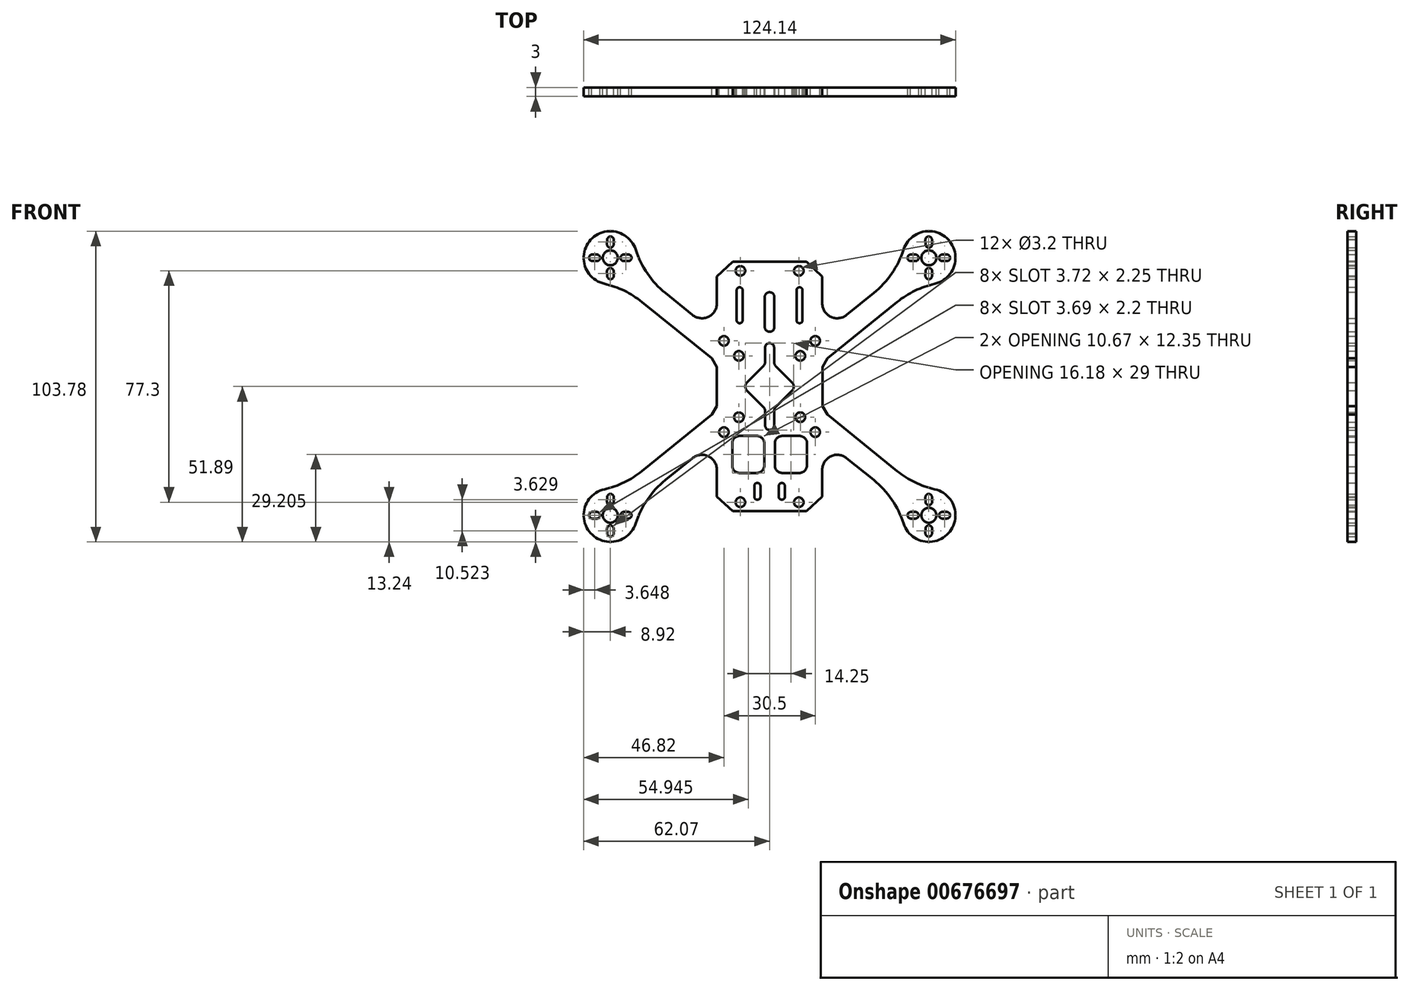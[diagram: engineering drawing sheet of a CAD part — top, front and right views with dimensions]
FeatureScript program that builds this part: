
annotation { "Feature Type Name" : "Feature", "Feature Type Description" : "" }
export const myFeature = defineFeature(function(context is Context, id is Id, definition is map)
    precondition{}
    {
        {
            var Q0;
            Q0=qCreatedBy(makeId("Front.planeOp"),FACE);
            var sketch = newSketch(context, id + "F0", { "sketchPlane" : qUnion([Q0])});
            skCircle(sketch, "E0", {"center": v(-53.17, 43) * mm, "radius": 2.5 * mm});
            skCircle(sketch, "E1", {"center": v(-53.17, 43) * mm, "radius": 4.5 * mm, "construction": true});
            skLineSegment(sketch, "E2", {"start": v(-53.17, 43) * mm, "end": v(-53.17, 56.5) * mm, "construction": true});
            skArc(sketch, "E3", {"start": v(-54.27, 47.54) * mm, "mid": v(-53.22, 46.4) * mm, "end": v(-52.08, 47.46) * mm});
            skLineSegment(sketch, "E4", {"start": v(-45.5, 43) * mm, "end": v(-53.17, 43) * mm, "construction": true});
            skArc(sketch, "E5", {"start": v(-57.69, 41.9) * mm, "mid": v(-56.58, 43) * mm, "end": v(-57.68, 44.1) * mm});
            skCircle(sketch, "E6.MirrorC", {"center": v(53.17, 43) * mm, "radius": 2.5 * mm});
            skCircle(sketch, "E7.MirrorC", {"center": v(-53.17, -43) * mm, "radius": 2.5 * mm});
            skCircle(sketch, "E8.MirrorC", {"center": v(53.17, -43) * mm, "radius": 2.5 * mm});
            skCircle(sketch, "E9", {"center": v(-53.17, 43) * mm, "radius": 40.64 * mm, "construction": true});
            skLineSegment(sketch, "E10", {"start": v(-53.17, 43) * mm, "end": v(53.17, -43) * mm, "construction": true});
            skCircle(sketch, "E11", {"center": v(-53.17, -43) * mm, "radius": 40.64 * mm, "construction": true});
            skCircle(sketch, "E12", {"center": v(53.17, 43) * mm, "radius": 40.64 * mm, "construction": true});
            skCircle(sketch, "E13", {"center": v(53.17, -43) * mm, "radius": 40.64 * mm, "construction": true});
            skPoint(sketch, "E14.visualSharp", {"position": v(-54.1, 37.74) * mm});
            skCircle(sketch, "E15", {"center": v(-53.17, 43) * mm, "radius": 7 * mm, "construction": true});
            skLineSegment(sketch, "E16", {"start": v(0, 0) * mm, "end": v(0, 56.66) * mm, "construction": true});
            skLineSegment(sketch, "E17", {"start": v(53.17, 43) * mm, "end": v(-53.17, -43) * mm, "construction": true});
            skPoint(sketch, "E18.visualSharp", {"position": v(-2.78, 0) * mm});
            skPoint(sketch, "E19.visualSharp", {"position": v(0, 2.87) * mm});
            skPoint(sketch, "E20.visualSharp", {"position": v(2.78, 0) * mm});
            skPoint(sketch, "E21.visualSharp", {"position": v(0, -2.87) * mm});
            skCircle(sketch, "E22", {"center": v(-10.25, 10.25) * mm, "radius": 1.6 * mm});
            skCircle(sketch, "E23.MirrorC", {"center": v(10.25, 10.25) * mm, "radius": 1.6 * mm});
            skCircle(sketch, "E24.MirrorC", {"center": v(-10.25, -10.25) * mm, "radius": 1.6 * mm});
            skCircle(sketch, "E25.MirrorC", {"center": v(10.25, -10.25) * mm, "radius": 1.6 * mm});
            skArc(sketch, "E26", {"start": v(0, 14.5) * mm, "mid": v(-1.06, 14.06) * mm, "end": v(-1.5, 13) * mm});
            skLineSegment(sketch, "E27", {"start": v(-1.5, 13) * mm, "end": v(-1.5, 11.17) * mm});
            skLineSegment(sketch, "E28.trimOffspring", {"start": v(-1.5, -11.66) * mm, "end": v(-1.5, -13) * mm});
            skLineSegment(sketch, "E29.filletArc", {"start": v(1.5, 11.27) * mm, "end": v(1.5, 11.27) * mm});
            skLineSegment(sketch, "E30.filletArc", {"start": v(1.5, -11.66) * mm, "end": v(1.5, -11.66) * mm});
            skLineSegment(sketch, "E31.filletArc", {"start": v(-1.5, -11.66) * mm, "end": v(-1.5, -11.66) * mm});
            skLineSegment(sketch, "E32", {"start": v(-1.5, 11.28) * mm, "end": v(-1.5, 8.22) * mm});
            skLineSegment(sketch, "E33.MirrorCS", {"start": v(1.5, 11.27) * mm, "end": v(1.5, 11.06) * mm});
            skPoint(sketch, "E34.visualSharp", {"position": v(-1.5, -11.66) * mm});
            skPoint(sketch, "E35.visualSharp", {"position": v(-1.5, 11.06) * mm});
            skPoint(sketch, "E36.newPointB", {"position": v(1.5, 11.06) * mm});
            skPoint(sketch, "E37.visualSharp", {"position": v(1.5, -11.66) * mm});
            skCircle(sketch, "E38", {"center": v(-53.17, 43) * mm, "radius": 8.8 * mm, "construction": true});
            skCircle(sketch, "E39", {"center": v(-53.17, 43) * mm, "radius": 6 * mm, "construction": true});
            skArc(sketch, "E40", {"start": v(-59.17, 44.1) * mm, "mid": v(-60.27, 43.11) * mm, "end": v(-59.4, 41.92) * mm});
            skLineSegment(sketch, "E41", {"start": v(-54.2, 49.2) * mm, "end": v(-54.27, 47.54) * mm});
            skLineSegment(sketch, "E42", {"start": v(-52.03, 49.01) * mm, "end": v(-52.08, 47.46) * mm});
            skLineSegment(sketch, "E43", {"start": v(-59.17, 44.1) * mm, "end": v(-57.68, 44.1) * mm});
            skLineSegment(sketch, "E44", {"start": v(-59.4, 41.92) * mm, "end": v(-57.69, 41.9) * mm});
            skArc(sketch, "E45.trimOffspring", {"start": v(-52.03, 49.01) * mm, "mid": v(-53.03, 50.12) * mm, "end": v(-54.2, 49.2) * mm});
            skArc(sketch, "E46.MirrorCS", {"start": v(-47.18, 44.1) * mm, "mid": v(-46.08, 43.11) * mm, "end": v(-46.96, 41.92) * mm});
            skArc(sketch, "E47.MirrorCS", {"start": v(-48.66, 41.9) * mm, "mid": v(-49.77, 43) * mm, "end": v(-48.67, 44.1) * mm});
            skLineSegment(sketch, "E48.MirrorCS", {"start": v(-47.18, 44.1) * mm, "end": v(-48.67, 44.1) * mm});
            skLineSegment(sketch, "E49.MirrorCS", {"start": v(-46.96, 41.92) * mm, "end": v(-48.66, 41.9) * mm});
            skLineSegment(sketch, "E50.MirrorCS", {"start": v(-52.03, 36.99) * mm, "end": v(-52.08, 38.54) * mm});
            skArc(sketch, "E51.MirrorCS", {"start": v(-52.03, 36.99) * mm, "mid": v(-53.03, 35.88) * mm, "end": v(-54.2, 36.8) * mm});
            skArc(sketch, "E52.MirrorCS", {"start": v(-54.27, 38.46) * mm, "mid": v(-53.22, 39.6) * mm, "end": v(-52.08, 38.54) * mm});
            skLineSegment(sketch, "E53.MirrorCS", {"start": v(-54.2, 36.8) * mm, "end": v(-54.27, 38.46) * mm});
            skLineSegment(sketch, "E54.MirrorCS", {"start": v(-52.03, -49.01) * mm, "end": v(-52.08, -47.46) * mm});
            skLineSegment(sketch, "E55.MirrorCS", {"start": v(-52.03, -36.99) * mm, "end": v(-52.08, -38.54) * mm});
            skLineSegment(sketch, "E56.MirrorCS", {"start": v(-59.4, -41.92) * mm, "end": v(-57.69, -41.9) * mm});
            skLineSegment(sketch, "E57.MirrorCS", {"start": v(-47.18, -44.1) * mm, "end": v(-48.67, -44.1) * mm});
            skLineSegment(sketch, "E58.MirrorCS", {"start": v(-59.17, -44.1) * mm, "end": v(-57.68, -44.1) * mm});
            skLineSegment(sketch, "E59.MirrorCS", {"start": v(-46.96, -41.92) * mm, "end": v(-48.66, -41.9) * mm});
            skLineSegment(sketch, "E60.MirrorCS", {"start": v(-54.2, -36.8) * mm, "end": v(-54.27, -38.46) * mm});
            skLineSegment(sketch, "E61.MirrorCS", {"start": v(-54.2, -49.2) * mm, "end": v(-54.27, -47.54) * mm});
            skArc(sketch, "E62.MirrorCS", {"start": v(-48.66, -41.9) * mm, "mid": v(-49.77, -43) * mm, "end": v(-48.67, -44.1) * mm});
            skArc(sketch, "E63.MirrorCS", {"start": v(-52.03, -49.01) * mm, "mid": v(-53.03, -50.12) * mm, "end": v(-54.2, -49.2) * mm});
            skArc(sketch, "E64.MirrorCS", {"start": v(-59.17, -44.1) * mm, "mid": v(-60.27, -43.11) * mm, "end": v(-59.4, -41.92) * mm});
            skArc(sketch, "E65.MirrorCS", {"start": v(-54.27, -47.54) * mm, "mid": v(-53.22, -46.4) * mm, "end": v(-52.08, -47.46) * mm});
            skLineSegment(sketch, "E66.MirrorCS", {"start": v(-45.5, -43) * mm, "end": v(-53.17, -43) * mm, "construction": true});
            skCircle(sketch, "E67.MirrorC", {"center": v(-53.17, -43) * mm, "radius": 6 * mm, "construction": true});
            skArc(sketch, "E68.MirrorCS", {"start": v(-57.69, -41.9) * mm, "mid": v(-56.58, -43) * mm, "end": v(-57.68, -44.1) * mm});
            skArc(sketch, "E69.MirrorCS", {"start": v(-47.18, -44.1) * mm, "mid": v(-46.08, -43.11) * mm, "end": v(-46.96, -41.92) * mm});
            skArc(sketch, "E70.MirrorCS", {"start": v(-54.27, -38.46) * mm, "mid": v(-53.22, -39.6) * mm, "end": v(-52.08, -38.54) * mm});
            skCircle(sketch, "E71.MirrorC", {"center": v(-53.17, -43) * mm, "radius": 4.5 * mm, "construction": true});
            skArc(sketch, "E72.MirrorCS", {"start": v(-52.03, -36.99) * mm, "mid": v(-53.03, -35.88) * mm, "end": v(-54.2, -36.8) * mm});
            skCircle(sketch, "E73.MirrorC", {"center": v(-53.17, -43) * mm, "radius": 7 * mm, "construction": true});
            skArc(sketch, "E74.MirrorCS", {"start": v(54.27, -38.46) * mm, "mid": v(53.22, -39.6) * mm, "end": v(52.08, -38.54) * mm});
            skLineSegment(sketch, "E75.MirrorCS", {"start": v(52.03, -49.01) * mm, "end": v(52.08, -47.46) * mm});
            skLineSegment(sketch, "E76.MirrorCS", {"start": v(47.18, -44.1) * mm, "end": v(48.67, -44.1) * mm});
            skArc(sketch, "E77.MirrorCS", {"start": v(48.66, -41.9) * mm, "mid": v(49.77, -43) * mm, "end": v(48.67, -44.1) * mm});
            skArc(sketch, "E78.MirrorCS", {"start": v(57.69, -41.9) * mm, "mid": v(56.58, -43) * mm, "end": v(57.68, -44.1) * mm});
            skLineSegment(sketch, "E79.MirrorCS", {"start": v(54.2, -36.8) * mm, "end": v(54.27, -38.46) * mm});
            skArc(sketch, "E80.MirrorCS", {"start": v(47.18, -44.1) * mm, "mid": v(46.08, -43.11) * mm, "end": v(46.96, -41.92) * mm});
            skLineSegment(sketch, "E81.MirrorCS", {"start": v(59.17, -44.1) * mm, "end": v(57.68, -44.1) * mm});
            skLineSegment(sketch, "E82.MirrorCS", {"start": v(54.2, -49.2) * mm, "end": v(54.27, -47.54) * mm});
            skArc(sketch, "E83.MirrorCS", {"start": v(54.27, -47.54) * mm, "mid": v(53.22, -46.4) * mm, "end": v(52.08, -47.46) * mm});
            skArc(sketch, "E84.MirrorCS", {"start": v(52.03, -49.01) * mm, "mid": v(53.03, -50.12) * mm, "end": v(54.2, -49.2) * mm});
            skLineSegment(sketch, "E85.MirrorCS", {"start": v(45.5, -43) * mm, "end": v(53.17, -43) * mm, "construction": true});
            skArc(sketch, "E86.MirrorCS", {"start": v(59.17, -44.1) * mm, "mid": v(60.27, -43.11) * mm, "end": v(59.4, -41.92) * mm});
            skLineSegment(sketch, "E87.MirrorCS", {"start": v(46.96, -41.92) * mm, "end": v(48.66, -41.9) * mm});
            skLineSegment(sketch, "E88.MirrorCS", {"start": v(52.03, -36.99) * mm, "end": v(52.08, -38.54) * mm});
            skLineSegment(sketch, "E89.MirrorCS", {"start": v(59.4, -41.92) * mm, "end": v(57.69, -41.9) * mm});
            skArc(sketch, "E90.MirrorCS", {"start": v(52.03, -36.99) * mm, "mid": v(53.03, -35.88) * mm, "end": v(54.2, -36.8) * mm});
            skLineSegment(sketch, "E91.MirrorCS", {"start": v(59.17, 44.1) * mm, "end": v(57.68, 44.1) * mm});
            skLineSegment(sketch, "E92.MirrorCS", {"start": v(47.18, 44.1) * mm, "end": v(48.67, 44.1) * mm});
            skArc(sketch, "E93.MirrorCS", {"start": v(47.18, 44.1) * mm, "mid": v(46.08, 43.11) * mm, "end": v(46.96, 41.92) * mm});
            skArc(sketch, "E94.MirrorCS", {"start": v(59.17, 44.1) * mm, "mid": v(60.27, 43.11) * mm, "end": v(59.4, 41.92) * mm});
            skLineSegment(sketch, "E95.MirrorCS", {"start": v(54.2, 49.2) * mm, "end": v(54.27, 47.54) * mm});
            skLineSegment(sketch, "E96.MirrorCS", {"start": v(59.4, 41.92) * mm, "end": v(57.69, 41.9) * mm});
            skArc(sketch, "E97.MirrorCS", {"start": v(48.66, 41.9) * mm, "mid": v(49.77, 43) * mm, "end": v(48.67, 44.1) * mm});
            skLineSegment(sketch, "E98.MirrorCS", {"start": v(45.5, 43) * mm, "end": v(53.17, 43) * mm, "construction": true});
            skArc(sketch, "E99.MirrorCS", {"start": v(52.03, 49.01) * mm, "mid": v(53.03, 50.12) * mm, "end": v(54.2, 49.2) * mm});
            skLineSegment(sketch, "E100.MirrorCS", {"start": v(52.03, 36.99) * mm, "end": v(52.08, 38.54) * mm});
            skArc(sketch, "E101.MirrorCS", {"start": v(52.03, 36.99) * mm, "mid": v(53.03, 35.88) * mm, "end": v(54.2, 36.8) * mm});
            skCircle(sketch, "E102.MirrorC", {"center": v(53.17, 43) * mm, "radius": 4.5 * mm, "construction": true});
            skArc(sketch, "E103.MirrorCS", {"start": v(54.27, 47.54) * mm, "mid": v(53.22, 46.4) * mm, "end": v(52.08, 47.46) * mm});
            skLineSegment(sketch, "E104.MirrorCS", {"start": v(46.96, 41.92) * mm, "end": v(48.66, 41.9) * mm});
            skArc(sketch, "E105.MirrorCS", {"start": v(57.69, 41.9) * mm, "mid": v(56.58, 43) * mm, "end": v(57.68, 44.1) * mm});
            skLineSegment(sketch, "E106.MirrorCS", {"start": v(52.03, 49.01) * mm, "end": v(52.08, 47.46) * mm});
            skLineSegment(sketch, "E107.MirrorCS", {"start": v(54.2, 36.8) * mm, "end": v(54.27, 38.46) * mm});
            skArc(sketch, "E108.MirrorCS", {"start": v(54.27, 38.46) * mm, "mid": v(53.22, 39.6) * mm, "end": v(52.08, 38.54) * mm});
            skCircle(sketch, "E109.MirrorC", {"center": v(53.17, -43) * mm, "radius": 4.5 * mm, "construction": true});
            skPoint(sketch, "E110.MirrorP", {"position": v(54.1, 37.74) * mm});
            skCircle(sketch, "E111.MirrorC", {"center": v(53.17, -43) * mm, "radius": 6 * mm, "construction": true});
            skCircle(sketch, "E112.MirrorC", {"center": v(53.17, -43) * mm, "radius": 7 * mm, "construction": true});
            skCircle(sketch, "E113.MirrorC", {"center": v(53.17, 43) * mm, "radius": 8.8 * mm, "construction": true});
            skCircle(sketch, "E114.MirrorC", {"center": v(53.17, 43) * mm, "radius": 7 * mm, "construction": true});
            skLineSegment(sketch, "E115.MirrorCS", {"start": v(53.17, 43) * mm, "end": v(53.17, 56.5) * mm, "construction": true});
            skCircle(sketch, "E116.MirrorC", {"center": v(53.17, 43) * mm, "radius": 6 * mm, "construction": true});
            skArc(sketch, "E117", {"start": v(-7.54, 1.38) * mm, "mid": v(-8.1, 0) * mm, "end": v(-7.54, -1.38) * mm});
            skLineSegment(sketch, "E118", {"start": v(-7.54, 1.38) * mm, "end": v(-2.09, 6.8) * mm});
            skLineSegment(sketch, "E119.MirrorCS", {"start": v(-7.54, -1.38) * mm, "end": v(-2.09, -6.8) * mm});
            skLineSegment(sketch, "E120", {"start": v(-1.5, -8.22) * mm, "end": v(-1.5, -11.66) * mm});
            skPoint(sketch, "E121.visualSharp", {"position": v(-1.5, 7.4) * mm});
            skArc(sketch, "E121.filletArc", {"start": v(-2.09, 6.8) * mm, "mid": v(-1.65, 7.46) * mm, "end": v(-1.5, 8.22) * mm});
            skPoint(sketch, "E122.visualSharp", {"position": v(1.5, 7.45) * mm});
            skPoint(sketch, "E123.visualSharp", {"position": v(-1.5, -7.4) * mm});
            skArc(sketch, "E123.filletArc", {"start": v(-1.5, -8.22) * mm, "mid": v(-1.65, -7.46) * mm, "end": v(-2.09, -6.8) * mm});
            skPoint(sketch, "E124.visualSharp", {"position": v(1.5, -7.45) * mm});
            skLineSegment(sketch, "E125", {"start": v(-15.72, 28.19) * mm, "end": v(-15.72, -29.81) * mm, "construction": true});
            skLineSegment(sketch, "E126", {"start": v(-15.72, -29.81) * mm, "end": v(15.28, -29.81) * mm, "construction": true});
            skLineSegment(sketch, "E127", {"start": v(15.28, -29.81) * mm, "end": v(15.28, 28.19) * mm, "construction": true});
            skLineSegment(sketch, "E128", {"start": v(15.28, 28.19) * mm, "end": v(-15.72, 28.19) * mm, "construction": true});
            skLineSegment(sketch, "E129", {"start": v(-35.66, 0) * mm, "end": v(24.54, 0) * mm, "construction": true});
            skCircle(sketch, "E130", {"center": v(-15.25, 15.25) * mm, "radius": 1.6 * mm});
            skCircle(sketch, "E131.MirrorC", {"center": v(15.25, 15.25) * mm, "radius": 1.6 * mm});
            skCircle(sketch, "E132.MirrorC", {"center": v(-15.25, -15.25) * mm, "radius": 1.6 * mm});
            skCircle(sketch, "E133.MirrorC", {"center": v(15.25, -15.25) * mm, "radius": 1.6 * mm});
            skCircle(sketch, "E134", {"center": v(-9.75, 38.65) * mm, "radius": 1.6 * mm});
            skCircle(sketch, "E135.MirrorC", {"center": v(9.75, 38.65) * mm, "radius": 1.6 * mm});
            skLineSegment(sketch, "E136", {"start": v(-17.58, 30.86) * mm, "end": v(-17.58, 36.82) * mm});
            skLineSegment(sketch, "E137", {"start": v(-17.58, 36.82) * mm, "end": v(-12.32, 41.66) * mm});
            skLineSegment(sketch, "E138", {"start": v(-12.32, 41.66) * mm, "end": v(0, 41.66) * mm});
            skCircle(sketch, "E139.MirrorC", {"center": v(-9.75, -38.65) * mm, "radius": 1.6 * mm});
            skCircle(sketch, "E140.MirrorC", {"center": v(9.75, -38.65) * mm, "radius": 1.6 * mm});
            skLineSegment(sketch, "E141.MirrorCS", {"start": v(12.32, 41.66) * mm, "end": v(0, 41.66) * mm});
            skLineSegment(sketch, "E142.MirrorCS", {"start": v(17.58, 36.82) * mm, "end": v(12.32, 41.66) * mm});
            skLineSegment(sketch, "E143.MirrorCS", {"start": v(17.58, 30.86) * mm, "end": v(17.58, 36.82) * mm});
            skLineSegment(sketch, "E144.MirrorCS", {"start": v(-17.58, -30.86) * mm, "end": v(-17.58, -36.82) * mm});
            skLineSegment(sketch, "E145.MirrorCS", {"start": v(-17.58, -36.82) * mm, "end": v(-12.32, -41.66) * mm});
            skLineSegment(sketch, "E146.MirrorCS", {"start": v(-12.32, -41.66) * mm, "end": v(0, -41.66) * mm});
            skLineSegment(sketch, "E147.MirrorCS", {"start": v(17.58, -36.82) * mm, "end": v(12.32, -41.66) * mm});
            skLineSegment(sketch, "E148.MirrorCS", {"start": v(17.58, -30.86) * mm, "end": v(17.58, -36.82) * mm});
            skLineSegment(sketch, "E149.MirrorCS", {"start": v(12.32, -41.66) * mm, "end": v(0, -41.66) * mm});
            skPoint(sketch, "E150.orphan", {"position": v(-17.58, 20.12) * mm});
            skPoint(sketch, "E151.visualSharp", {"position": v(-17.58, 20.84) * mm});
            skPoint(sketch, "E152.visualSharp", {"position": v(-22.6, 12.67) * mm});
            skPoint(sketch, "E153.orphan", {"position": v(17.58, 20.12) * mm});
            skPoint(sketch, "E154.MirrorCS.start.orphan", {"position": v(22.6, 12.67) * mm});
            skPoint(sketch, "E155.visualSharp", {"position": v(-71.74, 37.88) * mm});
            skPoint(sketch, "E156.visualSharp", {"position": v(-53.88, 61.73) * mm});
            skPoint(sketch, "E157.visualSharp", {"position": v(-17.58, 25.47) * mm});
            skPoint(sketch, "E158.orphan", {"position": v(17.58, 25.47) * mm});
            skArc(sketch, "E159", {"start": v(-10, -16.5) * mm, "mid": v(-11.6, -17.09) * mm, "end": v(-12.46, -18.56) * mm});
            skArc(sketch, "E160", {"start": v(-12.46, -26.8) * mm, "mid": v(-11.6, -28.28) * mm, "end": v(-10, -28.86) * mm});
            skLineSegment(sketch, "E161", {"start": v(-12.46, -18.56) * mm, "end": v(-12.46, -26.8) * mm});
            skArc(sketch, "E162", {"start": v(-1.8, -18.56) * mm, "mid": v(-2.66, -17.07) * mm, "end": v(-4.3, -16.5) * mm});
            skArc(sketch, "E163", {"start": v(-4.25, -28.86) * mm, "mid": v(-2.65, -28.28) * mm, "end": v(-1.8, -26.8) * mm});
            skLineSegment(sketch, "E164", {"start": v(-1.8, -18.56) * mm, "end": v(-1.8, -26.8) * mm});
            skArc(sketch, "E165.MirrorC", {"start": v(10, -16.5) * mm, "mid": v(11.6, -17.09) * mm, "end": v(12.46, -18.56) * mm});
            skArc(sketch, "E166.MirrorC", {"start": v(12.46, -26.8) * mm, "mid": v(11.59, -28.3) * mm, "end": v(9.96, -28.86) * mm});
            skLineSegment(sketch, "E167.MirrorCS", {"start": v(1.8, -18.56) * mm, "end": v(1.8, -26.8) * mm});
            skArc(sketch, "E168.MirrorC", {"start": v(4.25, -28.86) * mm, "mid": v(2.65, -28.28) * mm, "end": v(1.8, -26.8) * mm});
            skLineSegment(sketch, "E169.MirrorCS", {"start": v(12.46, -18.56) * mm, "end": v(12.46, -26.8) * mm});
            skArc(sketch, "E170.MirrorC", {"start": v(1.8, -18.56) * mm, "mid": v(2.65, -17.09) * mm, "end": v(4.25, -16.5) * mm});
            skPoint(sketch, "E171.orphan", {"position": v(-22.6, -12.67) * mm});
            skPoint(sketch, "E172.MirrorCS.end.orphan", {"position": v(-17.58, -20.12) * mm});
            skPoint(sketch, "E173.orphan", {"position": v(17.58, -20.12) * mm});
            skPoint(sketch, "E174.MirrorCS.start.orphan", {"position": v(22.6, -12.67) * mm});
            skPoint(sketch, "E175.orphan", {"position": v(-22.6, 0) * mm});
            skPoint(sketch, "E176.orphan", {"position": v(22.6, 0) * mm});
            skPoint(sketch, "E177.visualSharp", {"position": v(-22.6, 4.87) * mm});
            skPoint(sketch, "E178.visualSharp", {"position": v(-22.6, -4.87) * mm});
            skPoint(sketch, "E179.visualSharp", {"position": v(22.6, 4.87) * mm});
            skPoint(sketch, "E180.visualSharp", {"position": v(22.6, -4.87) * mm});
            skLineSegment(sketch, "E181.bottom", {"start": v(-4.1, -32.22) * mm, "end": v(-4.07, -32.22) * mm});
            skLineSegment(sketch, "E181.top", {"start": v(-4.1, -37.8) * mm, "end": v(-4.07, -37.8) * mm});
            skLineSegment(sketch, "E181.left", {"start": v(-5.1, -33.22) * mm, "end": v(-5.1, -36.8) * mm});
            skLineSegment(sketch, "E181.right", {"start": v(-3.07, -33.22) * mm, "end": v(-3.07, -36.8) * mm});
            skLineSegment(sketch, "E182.MirrorCS", {"start": v(4.1, -32.22) * mm, "end": v(4.07, -32.22) * mm});
            skLineSegment(sketch, "E183.MirrorCS", {"start": v(4.1, -37.8) * mm, "end": v(4.07, -37.8) * mm});
            skLineSegment(sketch, "E184.MirrorCS", {"start": v(5.1, -33.22) * mm, "end": v(5.1, -36.8) * mm});
            skLineSegment(sketch, "E185.MirrorCS", {"start": v(3.07, -33.22) * mm, "end": v(3.07, -36.8) * mm});
            skPoint(sketch, "E186.orphan", {"position": v(7.5, 1.41) * mm});
            skPoint(sketch, "E187.orphan", {"position": v(7.5, -1.41) * mm});
            skPoint(sketch, "E188.MirrorC.center.orphan", {"position": v(0, -13) * mm});
            skPoint(sketch, "E189.trimOffspring.end.orphan", {"position": v(1.5, -13) * mm});
            skArc(sketch, "E190.MirrorCS", {"start": v(0, 14.5) * mm, "mid": v(1.06, 14.06) * mm, "end": v(1.5, 13) * mm});
            skLineSegment(sketch, "E191.MirrorCS", {"start": v(1.5, 13) * mm, "end": v(1.5, 11.17) * mm});
            skLineSegment(sketch, "E192.MirrorCS", {"start": v(1.5, 11.28) * mm, "end": v(1.5, 8.22) * mm});
            skPoint(sketch, "E193.MirrorP", {"position": v(1.5, 7.4) * mm});
            skLineSegment(sketch, "E194.MirrorCS", {"start": v(7.54, 1.38) * mm, "end": v(2.09, 6.8) * mm});
            skArc(sketch, "E195.MirrorCS", {"start": v(7.54, 1.38) * mm, "mid": v(8.1, 0) * mm, "end": v(7.54, -1.38) * mm});
            skLineSegment(sketch, "E196.MirrorCS", {"start": v(7.54, -1.38) * mm, "end": v(2.09, -6.8) * mm});
            skArc(sketch, "E197.MirrorCS", {"start": v(1.5, -8.22) * mm, "mid": v(1.65, -7.46) * mm, "end": v(2.09, -6.8) * mm});
            skLineSegment(sketch, "E198.MirrorCS", {"start": v(1.5, -8.22) * mm, "end": v(1.5, -11.66) * mm});
            skArc(sketch, "E199.MirrorCS", {"start": v(2.09, 6.8) * mm, "mid": v(1.65, 7.46) * mm, "end": v(1.5, 8.22) * mm});
            skLineSegment(sketch, "E200.MirrorCS", {"start": v(1.5, -11.66) * mm, "end": v(1.5, -13) * mm});
            skArc(sketch, "E201.MirrorCS", {"start": v(0, -14.5) * mm, "mid": v(1.06, -14.06) * mm, "end": v(1.5, -13) * mm});
            skArc(sketch, "E202.MirrorCS", {"start": v(0, -14.5) * mm, "mid": v(-1.06, -14.06) * mm, "end": v(-1.5, -13) * mm});
            skPoint(sketch, "E203.visualSharp", {"position": v(-52.18, 59.42) * mm});
            skPoint(sketch, "E204.visualSharp", {"position": v(-69.03, 38.6) * mm});
            skPoint(sketch, "E152.filletArc.end.orphan", {"position": v(-23.63, 13.42) * mm});
            skPoint(sketch, "E152.filletArc.start.orphan", {"position": v(-22.6, 11.4) * mm});
            skPoint(sketch, "E205.MirrorCS.end.orphan", {"position": v(23.63, 13.42) * mm});
            skPoint(sketch, "E206.orphan", {"position": v(22.6, 11.4) * mm});
            skPoint(sketch, "E207.center.orphan", {"position": v(-18.5, 7.5) * mm});
            skPoint(sketch, "E208.MirrorCS.end.orphan", {"position": v(23.63, -13.42) * mm});
            skPoint(sketch, "E208.MirrorCS.start.orphan", {"position": v(22.6, -11.4) * mm});
            skPoint(sketch, "E209.MirrorCS.end.orphan", {"position": v(-23.63, -13.42) * mm});
            skPoint(sketch, "E209.MirrorCS.start.orphan", {"position": v(-22.6, -11.4) * mm});
            skArc(sketch, "E210", {"start": v(1.6, 29.9) * mm, "mid": v(0, 31.5) * mm, "end": v(-1.6, 29.9) * mm});
            skArc(sketch, "E211", {"start": v(-1.6, 19.9) * mm, "mid": v(0, 18.3) * mm, "end": v(1.6, 19.9) * mm});
            skLineSegment(sketch, "E212", {"start": v(-1.6, 29.9) * mm, "end": v(-1.6, 19.9) * mm});
            skLineSegment(sketch, "E213", {"start": v(1.6, 29.9) * mm, "end": v(1.6, 19.9) * mm});
            skPoint(sketch, "E214.center.orphan", {"position": v(0, 24.9) * mm});
            skPoint(sketch, "E215.firstSnap0", {"position": v(-17.58, 33.84) * mm});
            skLineSegment(sketch, "E215.bottom", {"start": v(-10, 33.15) * mm, "end": v(-10, 33.15) * mm});
            skLineSegment(sketch, "E215.top", {"start": v(-10, 21.15) * mm, "end": v(-10, 21.15) * mm});
            skLineSegment(sketch, "E215.left", {"start": v(-11, 32.15) * mm, "end": v(-11, 22.15) * mm});
            skLineSegment(sketch, "E215.right", {"start": v(-9, 32.15) * mm, "end": v(-9, 22.15) * mm});
            skPoint(sketch, "E216.visualSharp", {"position": v(-11, 33.15) * mm});
            skArc(sketch, "E216.filletArc", {"start": v(-10, 33.15) * mm, "mid": v(-10.7, 32.86) * mm, "end": v(-11, 32.15) * mm});
            skPoint(sketch, "E217.visualSharp", {"position": v(-9, 33.15) * mm});
            skArc(sketch, "E217.filletArc", {"start": v(-9, 32.15) * mm, "mid": v(-9.3, 32.86) * mm, "end": v(-10, 33.15) * mm});
            skPoint(sketch, "E218.visualSharp", {"position": v(-9, 21.15) * mm});
            skArc(sketch, "E218.filletArc", {"start": v(-10, 21.15) * mm, "mid": v(-9.3, 21.44) * mm, "end": v(-9, 22.15) * mm});
            skPoint(sketch, "E219.visualSharp", {"position": v(-11, 21.15) * mm});
            skArc(sketch, "E219.filletArc", {"start": v(-11, 22.15) * mm, "mid": v(-10.7, 21.44) * mm, "end": v(-10, 21.15) * mm});
            skArc(sketch, "E220.MirrorCS", {"start": v(11, 22.15) * mm, "mid": v(10.7, 21.44) * mm, "end": v(10, 21.15) * mm});
            skArc(sketch, "E221.MirrorCS", {"start": v(10, 21.15) * mm, "mid": v(9.3, 21.44) * mm, "end": v(9, 22.15) * mm});
            skArc(sketch, "E222.MirrorCS", {"start": v(9, 32.15) * mm, "mid": v(9.3, 32.86) * mm, "end": v(10, 33.15) * mm});
            skArc(sketch, "E223.MirrorCS", {"start": v(10, 33.15) * mm, "mid": v(10.7, 32.86) * mm, "end": v(11, 32.15) * mm});
            skLineSegment(sketch, "E224.MirrorCS", {"start": v(10, 21.15) * mm, "end": v(10, 21.15) * mm});
            skLineSegment(sketch, "E225.MirrorCS", {"start": v(10, 33.15) * mm, "end": v(10, 33.15) * mm});
            skPoint(sketch, "E226.MirrorP", {"position": v(11, 21.15) * mm});
            skLineSegment(sketch, "E227.MirrorCS", {"start": v(9, 32.15) * mm, "end": v(9, 22.15) * mm});
            skPoint(sketch, "E228.MirrorP", {"position": v(9, 21.15) * mm});
            skLineSegment(sketch, "E229.MirrorCS", {"start": v(11, 32.15) * mm, "end": v(11, 22.15) * mm});
            skPoint(sketch, "E230.MirrorP", {"position": v(9, 33.15) * mm});
            skPoint(sketch, "E231.MirrorP", {"position": v(11, 33.15) * mm});
            skPoint(sketch, "E232.MirrorCS.end.orphan", {"position": v(18.68, 0) * mm});
            skPoint(sketch, "E233.visualSharp", {"position": v(-5.1, -32.22) * mm});
            skArc(sketch, "E233.filletArc", {"start": v(-4.1, -32.22) * mm, "mid": v(-4.81, -32.52) * mm, "end": v(-5.1, -33.22) * mm});
            skPoint(sketch, "E234.visualSharp", {"position": v(-5.1, -37.8) * mm});
            skArc(sketch, "E234.filletArc", {"start": v(-5.1, -36.8) * mm, "mid": v(-4.81, -37.52) * mm, "end": v(-4.1, -37.8) * mm});
            skPoint(sketch, "E235.visualSharp", {"position": v(-3.07, -37.8) * mm});
            skArc(sketch, "E235.filletArc", {"start": v(-4.07, -37.8) * mm, "mid": v(-3.37, -37.52) * mm, "end": v(-3.07, -36.8) * mm});
            skPoint(sketch, "E236.visualSharp", {"position": v(-3.07, -32.22) * mm});
            skArc(sketch, "E236.filletArc", {"start": v(-3.07, -33.22) * mm, "mid": v(-3.37, -32.52) * mm, "end": v(-4.07, -32.22) * mm});
            skPoint(sketch, "E237.visualSharp", {"position": v(3.07, -32.22) * mm});
            skArc(sketch, "E237.filletArc", {"start": v(4.07, -32.22) * mm, "mid": v(3.37, -32.52) * mm, "end": v(3.07, -33.22) * mm});
            skPoint(sketch, "E238.visualSharp", {"position": v(5.1, -32.22) * mm});
            skArc(sketch, "E238.filletArc", {"start": v(5.1, -33.22) * mm, "mid": v(4.81, -32.52) * mm, "end": v(4.1, -32.22) * mm});
            skPoint(sketch, "E239.visualSharp", {"position": v(5.1, -37.8) * mm});
            skArc(sketch, "E239.filletArc", {"start": v(4.1, -37.8) * mm, "mid": v(4.81, -37.52) * mm, "end": v(5.1, -36.8) * mm});
            skPoint(sketch, "E240.visualSharp", {"position": v(3.07, -37.8) * mm});
            skArc(sketch, "E240.filletArc", {"start": v(3.07, -36.8) * mm, "mid": v(3.37, -37.52) * mm, "end": v(4.07, -37.8) * mm});
            skLineSegment(sketch, "E241", {"start": v(-10, -16.5) * mm, "end": v(-4.3, -16.5) * mm});
            skLineSegment(sketch, "E242", {"start": v(-10, -28.86) * mm, "end": v(-4.25, -28.86) * mm});
            skLineSegment(sketch, "E243", {"start": v(4.25, -16.5) * mm, "end": v(10, -16.5) * mm});
            skLineSegment(sketch, "E244", {"start": v(4.25, -28.86) * mm, "end": v(9.96, -28.86) * mm});
            skPoint(sketch, "E245.start.orphan", {"position": v(-6.7, -18.56) * mm});
            skPoint(sketch, "E246.start.orphan", {"position": v(-7.54, -18.56) * mm});
            skPoint(sketch, "E247.orphan", {"position": v(-7.54, -26.8) * mm});
            skPoint(sketch, "E248.orphan", {"position": v(-6.7, -26.8) * mm});
            skPoint(sketch, "E249.MirrorCS.start.orphan", {"position": v(7.54, -18.56) * mm});
            skPoint(sketch, "E250.MirrorCS.start.orphan", {"position": v(6.7, -18.56) * mm});
            skPoint(sketch, "E251.orphan", {"position": v(6.7, -26.8) * mm});
            skPoint(sketch, "E252.orphan", {"position": v(7.54, -26.8) * mm});
            skArc(sketch, "E253", {"start": v(-44.7, 45.72) * mm, "mid": v(-59.73, 49) * mm, "end": v(-55.14, 34.33) * mm});
            skLineSegment(sketch, "E254", {"start": v(-17.58, 30.86) * mm, "end": v(-17.6, 27.78) * mm});
            skPoint(sketch, "E255.MirrorCS.end.orphan", {"position": v(-20.7, 13.62) * mm});
            skPoint(sketch, "E256.orphan", {"position": v(-48.04, 35.74) * mm});
            skLineSegment(sketch, "E257.trimOffspring", {"start": v(-17.65, 6.55) * mm, "end": v(-17.65, -6.55) * mm});
            skLineSegment(sketch, "E258", {"start": v(-19.3, 9.4) * mm, "end": v(-17.65, 6.55) * mm});
            skLineSegment(sketch, "E259.MirrorCS", {"start": v(-42.63, -28.26) * mm, "end": v(-19.3, -9.4) * mm});
            skLineSegment(sketch, "E260.MirrorCS", {"start": v(-34.79, -31.24) * mm, "end": v(-25.74, -23.92) * mm});
            skLineSegment(sketch, "E261.MirrorCS", {"start": v(-19.3, -9.4) * mm, "end": v(-17.65, -6.55) * mm});
            skLineSegment(sketch, "E262.MirrorCS", {"start": v(-17.58, -30.86) * mm, "end": v(-17.6, -27.78) * mm});
            skArc(sketch, "E263.MirrorCS", {"start": v(-44.7, -45.72) * mm, "mid": v(-59.73, -49) * mm, "end": v(-55.14, -34.33) * mm});
            skLineSegment(sketch, "E264.MirrorCS", {"start": v(42.63, 28.26) * mm, "end": v(19.3, 9.4) * mm});
            skLineSegment(sketch, "E265.MirrorCS", {"start": v(17.58, 30.86) * mm, "end": v(17.6, 27.78) * mm});
            skLineSegment(sketch, "E266.MirrorCS", {"start": v(19.3, 9.4) * mm, "end": v(17.65, 6.55) * mm});
            skLineSegment(sketch, "E267.MirrorCS", {"start": v(17.65, 6.55) * mm, "end": v(17.65, -6.55) * mm});
            skLineSegment(sketch, "E268.MirrorCS", {"start": v(19.3, -9.4) * mm, "end": v(17.65, -6.55) * mm});
            skLineSegment(sketch, "E269.MirrorCS", {"start": v(42.63, -28.26) * mm, "end": v(19.3, -9.4) * mm});
            skLineSegment(sketch, "E270.MirrorCS", {"start": v(34.79, -31.24) * mm, "end": v(25.74, -23.92) * mm});
            skArc(sketch, "E271.MirrorCS", {"start": v(44.7, -45.72) * mm, "mid": v(59.73, -49) * mm, "end": v(55.14, -34.33) * mm});
            skLineSegment(sketch, "E272.MirrorCS", {"start": v(17.58, -30.86) * mm, "end": v(17.6, -27.78) * mm});
            skPoint(sketch, "E273.orphan", {"position": v(-17.65, -10.17) * mm});
            skPoint(sketch, "E274.orphan", {"position": v(17.65, -10.17) * mm});
            skArc(sketch, "E275.MirrorCS", {"start": v(44.7, 45.72) * mm, "mid": v(59.73, 49) * mm, "end": v(55.14, 34.33) * mm});
            skPoint(sketch, "E276.visualSharp", {"position": v(-45, 39.5) * mm});
            skPoint(sketch, "E277.visualSharp", {"position": v(-17.65, 17.38) * mm});
            skArc(sketch, "E277.filletArc", {"start": v(-25.74, 23.92) * mm, "mid": v(-20.45, 23.3) * mm, "end": v(-17.6, 27.78) * mm});
            skPoint(sketch, "E278.visualSharp", {"position": v(17.65, 17.38) * mm});
            skArc(sketch, "E278.filletArc", {"start": v(17.6, 27.78) * mm, "mid": v(20.45, 23.3) * mm, "end": v(25.74, 23.92) * mm});
            skPoint(sketch, "E279.visualSharp", {"position": v(17.65, -17.38) * mm});
            skArc(sketch, "E279.filletArc", {"start": v(25.74, -23.92) * mm, "mid": v(20.45, -23.3) * mm, "end": v(17.6, -27.78) * mm});
            skPoint(sketch, "E280.visualSharp", {"position": v(-17.65, -17.38) * mm});
            skArc(sketch, "E280.filletArc", {"start": v(-17.6, -27.78) * mm, "mid": v(-20.45, -23.3) * mm, "end": v(-25.74, -23.92) * mm});
            skPoint(sketch, "E281.visualSharp", {"position": v(-50.4, 34.55) * mm});
            skPoint(sketch, "E282.visualSharp", {"position": v(45, 39.5) * mm});
            skPoint(sketch, "E283.visualSharp", {"position": v(-50.4, -34.55) * mm});
            skArc(sketch, "E283.filletArc", {"start": v(-55.14, -34.33) * mm, "mid": v(-48.54, -32.01) * mm, "end": v(-42.63, -28.26) * mm});
            skPoint(sketch, "E284.visualSharp", {"position": v(50.4, 34.55) * mm});
            skArc(sketch, "E284.filletArc", {"start": v(55.14, 34.33) * mm, "mid": v(48.54, 32.01) * mm, "end": v(42.63, 28.26) * mm});
            skPoint(sketch, "E285.visualSharp", {"position": v(50.4, -34.55) * mm});
            skArc(sketch, "E285.filletArc", {"start": v(42.63, -28.26) * mm, "mid": v(48.54, -32.01) * mm, "end": v(55.14, -34.33) * mm});
            skPoint(sketch, "E286.visualSharp", {"position": v(45, -39.5) * mm});
            skArc(sketch, "E286.filletArc", {"start": v(44.7, -45.72) * mm, "mid": v(40.8, -37.76) * mm, "end": v(34.79, -31.24) * mm});
            skArc(sketch, "E287.MirrorCS", {"start": v(-55.14, 34.33) * mm, "mid": v(-48.54, 32.01) * mm, "end": v(-42.63, 28.26) * mm});
            skLineSegment(sketch, "E288.MirrorCS", {"start": v(-42.63, 28.26) * mm, "end": v(-19.3, 9.4) * mm});
            skPoint(sketch, "E289.visualSharp", {"position": v(-45, -39.5) * mm});
            skArc(sketch, "E289.filletArc", {"start": v(-34.79, -31.24) * mm, "mid": v(-40.8, -37.76) * mm, "end": v(-44.7, -45.72) * mm});
            skArc(sketch, "E290.MirrorCS", {"start": v(-34.79, 31.24) * mm, "mid": v(-40.8, 37.76) * mm, "end": v(-44.7, 45.72) * mm});
            skLineSegment(sketch, "E291.MirrorCS", {"start": v(-34.79, 31.24) * mm, "end": v(-25.74, 23.92) * mm});
            skArc(sketch, "E292.MirrorCS", {"start": v(44.7, 45.72) * mm, "mid": v(40.8, 37.76) * mm, "end": v(34.79, 31.24) * mm});
            skLineSegment(sketch, "E293.MirrorCS", {"start": v(34.79, 31.24) * mm, "end": v(25.74, 23.92) * mm});
            skSolve(sketch);
        }
        {
            var Q0;
            Q0 = qSketchRegion(id + "F0", true);
            extrude(context, id + "F1", {"entities" : qUnion([Q0]), "depth" : 3 * mm, "offsetDistance" : 25 * mm});
        }
    });
